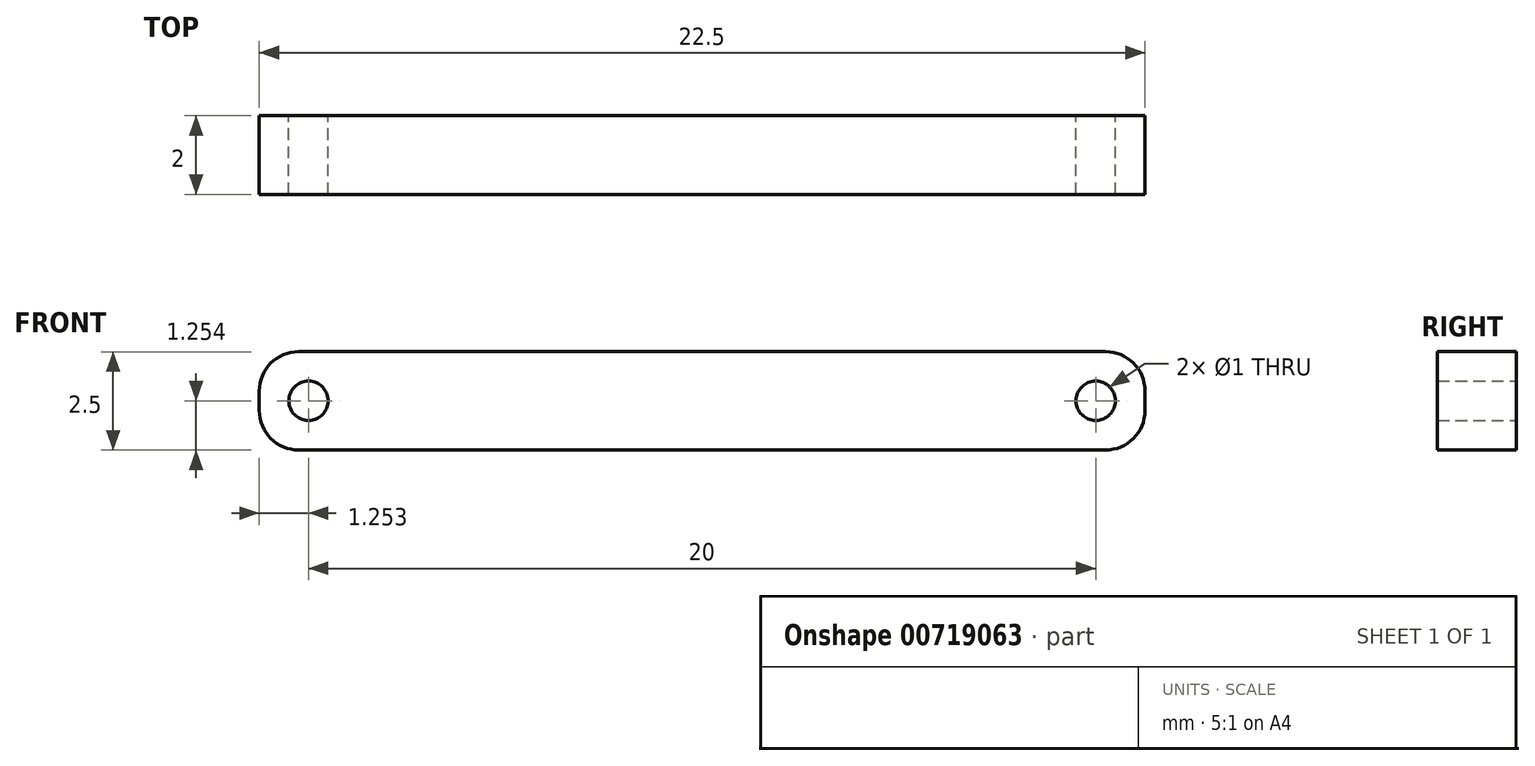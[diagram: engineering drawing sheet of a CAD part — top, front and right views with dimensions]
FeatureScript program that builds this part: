
annotation { "Feature Type Name" : "Feature", "Feature Type Description" : "" }
export const myFeature = defineFeature(function(context is Context, id is Id, definition is map)
    precondition{}
    {
        {
            var Q0;
            Q0=qCreatedBy(makeId("Front.planeOp"),FACE);
            var sketch = newSketch(context, id + "F0", { "sketchPlane" : qUnion([Q0])});
            skLineSegment(sketch, "E0.bottom", {"start": v(-0.8, -0.78) * mm, "end": v(19.7, -0.78) * mm});
            skLineSegment(sketch, "E0.top", {"start": v(-0.8, -3.28) * mm, "end": v(19.7, -3.28) * mm});
            skLineSegment(sketch, "E0.left", {"start": v(-1.8, -1.78) * mm, "end": v(-1.8, -2.28) * mm});
            skLineSegment(sketch, "E0.right", {"start": v(20.7, -1.78) * mm, "end": v(20.7, -2.28) * mm});
            skCircle(sketch, "E1", {"center": v(19.44, -2.03) * mm, "radius": 0.5 * mm});
            skCircle(sketch, "E2", {"center": v(-0.56, -2.03) * mm, "radius": 0.5 * mm});
            skPoint(sketch, "E3.visualSharp", {"position": v(-1.8, -0.78) * mm});
            skArc(sketch, "E3.filletArc", {"start": v(-0.8, -0.78) * mm, "mid": v(-1.51, -1.07) * mm, "end": v(-1.8, -1.78) * mm});
            skPoint(sketch, "E4.visualSharp", {"position": v(-1.8, -3.28) * mm});
            skArc(sketch, "E4.filletArc", {"start": v(-1.8, -2.28) * mm, "mid": v(-1.51, -2.98) * mm, "end": v(-0.8, -3.28) * mm});
            skPoint(sketch, "E5.visualSharp", {"position": v(20.7, -0.78) * mm});
            skArc(sketch, "E5.filletArc", {"start": v(20.7, -1.78) * mm, "mid": v(20.4, -1.07) * mm, "end": v(19.7, -0.78) * mm});
            skPoint(sketch, "E6.visualSharp", {"position": v(20.7, -3.28) * mm});
            skArc(sketch, "E6.filletArc", {"start": v(19.7, -3.28) * mm, "mid": v(20.4, -2.98) * mm, "end": v(20.7, -2.28) * mm});
            skSolve(sketch);
        }
        {
            var Q0;
            Q0=makeQuery(id+"F0.imprint","IMPRINT",FACE,{"disambiguationData":[TD([[makeQuery(id+"F0.imprint","IMPRINT",EDGE,{"derivedFrom":sQuery(id+"F0.wireOp",EDGE,"E0.bottom")}),-1.0]])]});
            extrude(context, id + "F1", {"entities" : qUnion([Q0]), "depth" : 2 * mm, "offsetDistance" : 25 * mm});
        }
    });
